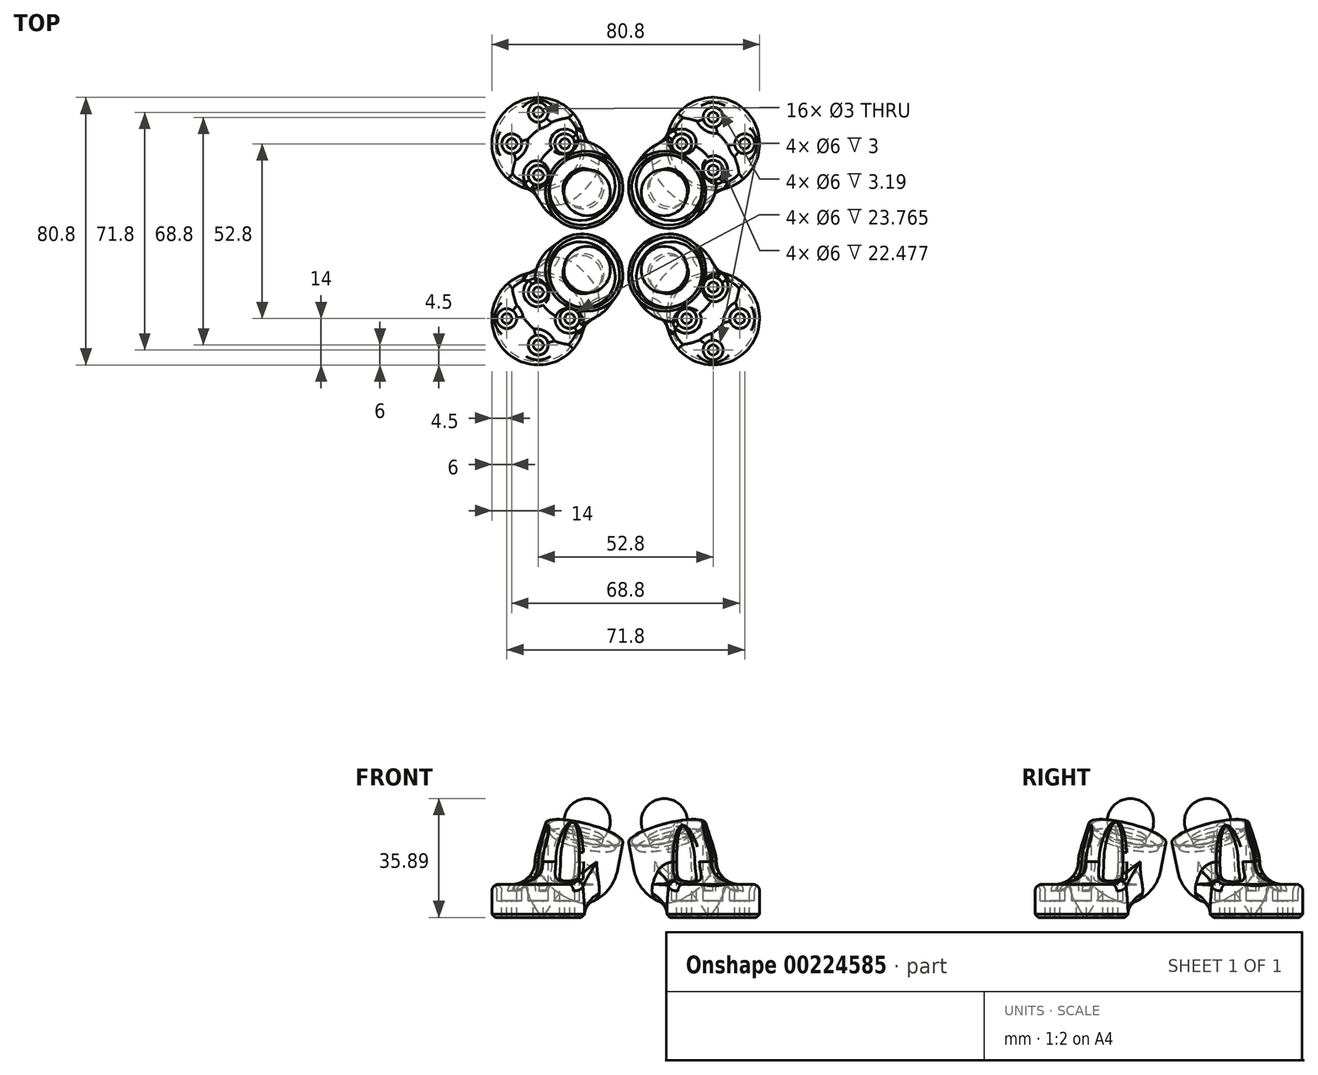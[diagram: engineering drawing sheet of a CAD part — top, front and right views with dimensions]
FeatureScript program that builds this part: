
annotation { "Feature Type Name" : "Feature", "Feature Type Description" : "" }
export const myFeature = defineFeature(function(context is Context, id is Id, definition is map)
    precondition{}
    {
        {
            var Q0;
            Q0=qCreatedBy(makeId("Top.planeOp"),FACE);
            var sketch = newSketch(context, id + "F0", { "sketchPlane" : qUnion([Q0])});
            skLineSegment(sketch, "E0", {"start": v(-39.6, -39.1) * mm, "end": v(-39.6, -104.05) * mm, "construction": true});
            skLineSegment(sketch, "E1", {"start": v(-66.97, -39.6) * mm, "end": v(-8.74, -39.6) * mm, "construction": true});
            skCircle(sketch, "E2", {"center": v(-39.6, -31.6) * mm, "radius": 1.5 * mm});
            skCircle(sketch, "E3", {"center": v(-39.6, -47.6) * mm, "radius": 1.5 * mm});
            skCircle(sketch, "E4", {"center": v(-49.1, -39.6) * mm, "radius": 1.5 * mm});
            skCircle(sketch, "E5", {"center": v(-30.1, -39.6) * mm, "radius": 1.5 * mm});
            skCircle(sketch, "E6", {"center": v(-39.6, -39.6) * mm, "radius": 14 * mm});
            skCircle(sketch, "E7", {"center": v(-49.1, -39.6) * mm, "radius": 3 * mm});
            skCircle(sketch, "E8", {"center": v(-39.6, -47.6) * mm, "radius": 3 * mm});
            skCircle(sketch, "E9", {"center": v(-30.1, -39.6) * mm, "radius": 3 * mm});
            skCircle(sketch, "E10", {"center": v(-39.6, -31.6) * mm, "radius": 3 * mm});
            skSolve(sketch);
        }
        {
            var Q0;
            Q0=qCreatedBy(makeId("Top.planeOp"),FACE);
            var sketch = newSketch(context, id + "F1", { "sketchPlane" : qUnion([Q0])});
            skLineSegment(sketch, "E11.bottom", {"start": v(53, -53) * mm, "end": v(-53, -53) * mm, "construction": true});
            skLineSegment(sketch, "E11.top", {"start": v(53, 53) * mm, "end": v(-53, 53) * mm, "construction": true});
            skLineSegment(sketch, "E11.left", {"start": v(53, -53) * mm, "end": v(53, 53) * mm, "construction": true});
            skLineSegment(sketch, "E11.right", {"start": v(-53, -53) * mm, "end": v(-53, 53) * mm, "construction": true});
            skPoint(sketch, "E11.middle", {"position": v(0, 0) * mm});
            skLineSegment(sketch, "E12", {"start": v(53, 53) * mm, "end": v(-53, -53) * mm, "construction": true});
            skLineSegment(sketch, "E13", {"start": v(-53, 53) * mm, "end": v(53, -53) * mm, "construction": true});
            skCircle(sketch, "E14", {"center": v(53, 38) * mm, "radius": 3 * mm});
            skCircle(sketch, "E15", {"center": v(53, 38) * mm, "radius": 1.4 * mm});
            skLineSegment(sketch, "E16", {"start": v(53, 38) * mm, "end": v(57.2, 42.2) * mm, "construction": true});
            skLineSegment(sketch, "E17", {"start": v(57.2, 0) * mm, "end": v(57.2, 42.2) * mm});
            skLineSegment(sketch, "E18", {"start": v(53, 38) * mm, "end": v(49.8, 34.8) * mm, "construction": true});
            skLineSegment(sketch, "E19", {"start": v(49.8, 0) * mm, "end": v(49.8, 34.8) * mm});
            skPoint(sketch, "E19.startSnap0", {"position": v(53, 0) * mm});
            skLineSegment(sketch, "E20", {"start": v(57.2, 42.2) * mm, "end": v(49.7, 49.7) * mm});
            skLineSegment(sketch, "E21", {"start": v(49.8, 34.8) * mm, "end": v(42.3, 42.3) * mm});
            skLineSegment(sketch, "E22", {"start": v(53, 38) * mm, "end": v(45.5, 45.5) * mm, "construction": true});
            skLineSegment(sketch, "E23.MirrorCS", {"start": v(42.2, 57.2) * mm, "end": v(49.7, 49.7) * mm});
            skLineSegment(sketch, "E24.MirrorCS", {"start": v(0, 49.8) * mm, "end": v(34.8, 49.8) * mm});
            skPoint(sketch, "E25.MirrorP", {"position": v(0, 53) * mm});
            skLineSegment(sketch, "E26.MirrorCS", {"start": v(0, 57.2) * mm, "end": v(42.2, 57.2) * mm});
            skLineSegment(sketch, "E27.MirrorCS", {"start": v(34.8, 49.8) * mm, "end": v(42.3, 42.3) * mm});
            skCircle(sketch, "E28.MirrorC", {"center": v(38, 53) * mm, "radius": 3 * mm});
            skCircle(sketch, "E29.MirrorC", {"center": v(38, 53) * mm, "radius": 1.4 * mm});
            skLineSegment(sketch, "E30.MirrorCS", {"start": v(38, 53) * mm, "end": v(34.8, 49.8) * mm, "construction": true});
            skLineSegment(sketch, "E31.MirrorCS", {"start": v(38, 53) * mm, "end": v(42.2, 57.2) * mm, "construction": true});
            skLineSegment(sketch, "E32.MirrorCS", {"start": v(38, 53) * mm, "end": v(45.5, 45.5) * mm, "construction": true});
            skCircle(sketch, "E33.MirrorC", {"center": v(-53, 38) * mm, "radius": 1.4 * mm});
            skCircle(sketch, "E34.MirrorC", {"center": v(-38, 53) * mm, "radius": 1.4 * mm});
            skLineSegment(sketch, "E35.MirrorCS", {"start": v(-38, 53) * mm, "end": v(-34.8, 49.8) * mm, "construction": true});
            skLineSegment(sketch, "E36.MirrorCS", {"start": v(-53, 38) * mm, "end": v(-49.8, 34.8) * mm, "construction": true});
            skLineSegment(sketch, "E37.MirrorCS", {"start": v(-53, 38) * mm, "end": v(-57.2, 42.2) * mm, "construction": true});
            skLineSegment(sketch, "E38.MirrorCS", {"start": v(-38, 53) * mm, "end": v(-42.2, 57.2) * mm, "construction": true});
            skLineSegment(sketch, "E39.MirrorCS", {"start": v(0, 49.8) * mm, "end": v(-34.8, 49.8) * mm});
            skLineSegment(sketch, "E40.MirrorCS", {"start": v(-49.8, 0) * mm, "end": v(-49.8, 34.8) * mm});
            skLineSegment(sketch, "E41.MirrorCS", {"start": v(-34.8, 49.8) * mm, "end": v(-42.3, 42.3) * mm});
            skLineSegment(sketch, "E42.MirrorCS", {"start": v(-57.2, 42.2) * mm, "end": v(-49.7, 49.7) * mm});
            skLineSegment(sketch, "E43.MirrorCS", {"start": v(-57.2, 0) * mm, "end": v(-57.2, 42.2) * mm});
            skLineSegment(sketch, "E44.MirrorCS", {"start": v(0, 57.2) * mm, "end": v(-42.2, 57.2) * mm});
            skLineSegment(sketch, "E45.MirrorCS", {"start": v(-42.2, 57.2) * mm, "end": v(-49.7, 49.7) * mm});
            skCircle(sketch, "E46.MirrorC", {"center": v(-53, 38) * mm, "radius": 3 * mm});
            skLineSegment(sketch, "E47.MirrorCS", {"start": v(-49.8, 34.8) * mm, "end": v(-42.3, 42.3) * mm});
            skPoint(sketch, "E48.MirrorP", {"position": v(-53, 0) * mm});
            skCircle(sketch, "E49.MirrorC", {"center": v(-38, 53) * mm, "radius": 3 * mm});
            skLineSegment(sketch, "E50.MirrorCS", {"start": v(-53, 38) * mm, "end": v(-45.5, 45.5) * mm, "construction": true});
            skLineSegment(sketch, "E51.MirrorCS", {"start": v(-38, 53) * mm, "end": v(-45.5, 45.5) * mm, "construction": true});
            skCircle(sketch, "E52.MirrorC", {"center": v(-38, -53) * mm, "radius": 1.4 * mm});
            skCircle(sketch, "E53.MirrorC", {"center": v(-53, -38) * mm, "radius": 1.4 * mm});
            skCircle(sketch, "E54.MirrorC", {"center": v(38, -53) * mm, "radius": 1.4 * mm});
            skCircle(sketch, "E55.MirrorC", {"center": v(53, -38) * mm, "radius": 1.4 * mm});
            skLineSegment(sketch, "E56.MirrorCS", {"start": v(-38, -53) * mm, "end": v(-34.8, -49.8) * mm, "construction": true});
            skLineSegment(sketch, "E57.MirrorCS", {"start": v(-53, -38) * mm, "end": v(-49.8, -34.8) * mm, "construction": true});
            skLineSegment(sketch, "E58.MirrorCS", {"start": v(38, -53) * mm, "end": v(34.8, -49.8) * mm, "construction": true});
            skLineSegment(sketch, "E59.MirrorCS", {"start": v(53, -38) * mm, "end": v(49.8, -34.8) * mm, "construction": true});
            skLineSegment(sketch, "E60.MirrorCS", {"start": v(-53, -38) * mm, "end": v(-57.2, -42.2) * mm, "construction": true});
            skLineSegment(sketch, "E61.MirrorCS", {"start": v(38, -53) * mm, "end": v(42.2, -57.2) * mm, "construction": true});
            skLineSegment(sketch, "E62.MirrorCS", {"start": v(53, -38) * mm, "end": v(57.2, -42.2) * mm, "construction": true});
            skLineSegment(sketch, "E63.MirrorCS", {"start": v(-38, -53) * mm, "end": v(-42.2, -57.2) * mm, "construction": true});
            skPoint(sketch, "E64.MirrorP", {"position": v(0, -53) * mm});
            skLineSegment(sketch, "E65.MirrorCS", {"start": v(0, -49.8) * mm, "end": v(34.8, -49.8) * mm});
            skLineSegment(sketch, "E66.MirrorCS", {"start": v(0, -49.8) * mm, "end": v(-34.8, -49.8) * mm});
            skLineSegment(sketch, "E67.MirrorCS", {"start": v(-49.8, 0) * mm, "end": v(-49.8, -34.8) * mm});
            skLineSegment(sketch, "E68.MirrorCS", {"start": v(49.8, 0) * mm, "end": v(49.8, -34.8) * mm});
            skLineSegment(sketch, "E69.MirrorCS", {"start": v(-49.8, -34.8) * mm, "end": v(-42.3, -42.3) * mm});
            skCircle(sketch, "E70.MirrorC", {"center": v(-53, -38) * mm, "radius": 3 * mm});
            skCircle(sketch, "E71.MirrorC", {"center": v(38, -53) * mm, "radius": 3 * mm});
            skLineSegment(sketch, "E72.MirrorCS", {"start": v(57.2, -42.2) * mm, "end": v(49.7, -49.7) * mm});
            skLineSegment(sketch, "E73.MirrorCS", {"start": v(49.8, -34.8) * mm, "end": v(42.3, -42.3) * mm});
            skCircle(sketch, "E74.MirrorC", {"center": v(53, -38) * mm, "radius": 3 * mm});
            skLineSegment(sketch, "E75.MirrorCS", {"start": v(-42.2, -57.2) * mm, "end": v(-49.7, -49.7) * mm});
            skLineSegment(sketch, "E76.MirrorCS", {"start": v(57.2, 0) * mm, "end": v(57.2, -42.2) * mm});
            skCircle(sketch, "E77.MirrorC", {"center": v(-38, -53) * mm, "radius": 3 * mm});
            skLineSegment(sketch, "E78.MirrorCS", {"start": v(-57.2, -42.2) * mm, "end": v(-49.7, -49.7) * mm});
            skLineSegment(sketch, "E79.MirrorCS", {"start": v(42.2, -57.2) * mm, "end": v(49.7, -49.7) * mm});
            skLineSegment(sketch, "E80.MirrorCS", {"start": v(0, -57.2) * mm, "end": v(-42.2, -57.2) * mm});
            skLineSegment(sketch, "E81.MirrorCS", {"start": v(-34.8, -49.8) * mm, "end": v(-42.3, -42.3) * mm});
            skLineSegment(sketch, "E82.MirrorCS", {"start": v(34.8, -49.8) * mm, "end": v(42.3, -42.3) * mm});
            skLineSegment(sketch, "E83.MirrorCS", {"start": v(-57.2, 0) * mm, "end": v(-57.2, -42.2) * mm});
            skLineSegment(sketch, "E84.MirrorCS", {"start": v(0, -57.2) * mm, "end": v(42.2, -57.2) * mm});
            skLineSegment(sketch, "E85.MirrorCS", {"start": v(-38, -53) * mm, "end": v(-45.5, -45.5) * mm, "construction": true});
            skLineSegment(sketch, "E86.MirrorCS", {"start": v(-53, -38) * mm, "end": v(-45.5, -45.5) * mm, "construction": true});
            skLineSegment(sketch, "E87.MirrorCS", {"start": v(53, -38) * mm, "end": v(45.5, -45.5) * mm, "construction": true});
            skLineSegment(sketch, "E88.MirrorCS", {"start": v(38, -53) * mm, "end": v(45.5, -45.5) * mm, "construction": true});
            skLineSegment(sketch, "E89", {"start": v(34.8, -49.8) * mm, "end": v(34.8, -57.2) * mm});
            skLineSegment(sketch, "E90", {"start": v(34.8, 49.8) * mm, "end": v(34.8, 57.2) * mm});
            skLineSegment(sketch, "E91", {"start": v(-34.8, 49.8) * mm, "end": v(-34.8, 57.2) * mm});
            skLineSegment(sketch, "E92", {"start": v(-34.8, -49.8) * mm, "end": v(-34.8, -57.2) * mm});
            skLineSegment(sketch, "E93", {"start": v(-42.3, 42.3) * mm, "end": v(-42.3, -42.3) * mm});
            skSolve(sketch);
        }
        {
            var Q0;
            Q0=qCreatedBy(makeId("Front.planeOp"),FACE);
            var sketch = newSketch(context, id + "F2", { "sketchPlane" : qUnion([Q0])});
            skLineSegment(sketch, "E94", {"start": v(0, 0) * mm, "end": v(0, 2) * mm});
            skSolve(sketch);
        }
        {
            var Q0;
            Q0=sQuery(id+"F2.wireOp",EDGE,"E94");
            extrude(context, id + "F3", {"bodyType" : ExtendedToolBodyType.SURFACE, "surfaceEntities" : qUnion([Q0]), "depth" : 1 * mm});
        }
        {
            var Q0;
            Q0=qCreatedBy(makeId("Front.planeOp"),FACE);
            var Q1;
            Q1=sQuery(id+"F2.wireOp",EDGE,"E94");
            cPlane(context, id + "F4", {"entities" : qUnion([Q0, Q1]), "cplaneType" : CPlaneType.LINE_ANGLE, "offset" : 25 * mm, "angle" : 45 * degree, "width" : 150 * mm, "height" : 150 * mm});
        }
        {
            var Q0;
            Q0=qCreatedBy(id+"F4.planeOp",FACE);
            var sketch = newSketch(context, id + "F5", { "sketchPlane" : qUnion([Q0])});
            skLineSegment(sketch, "E95", {"start": v(-2, 0) * mm, "end": v(0, 0) * mm});
            skSolve(sketch);
        }
        {
            var Q0;
            Q0=qCreatedBy(id+"F4.planeOp",FACE);
            var sketch = newSketch(context, id + "F6", { "sketchPlane" : qUnion([Q0])});
            skLineSegment(sketch, "E96", {"start": v(70, 0) * mm, "end": v(70, 20) * mm, "construction": true});
            skCircle(sketch, "E97", {"center": v(70, 20) * mm, "radius": 7 * mm});
            skLineSegment(sketch, "E98", {"start": v(70, 0) * mm, "end": v(70, 15.12) * mm});
            skLineSegment(sketch, "E99", {"start": v(70, -15.12) * mm, "end": v(70, -15.12) * mm});
            skLineSegment(sketch, "E100", {"start": v(70, 15.12) * mm, "end": v(70, 27) * mm});
            skArc(sketch, "E101", {"start": v(70, -5.87) * mm, "mid": v(81.14, 0.97) * mm, "end": v(80.2, 14) * mm});
            skLineSegment(sketch, "E102", {"start": v(76, 9.37) * mm, "end": v(76, 16.4) * mm});
            skLineSegment(sketch, "E103", {"start": v(80.2, 14) * mm, "end": v(76, 14) * mm});
            skLineSegment(sketch, "E104", {"start": v(76, 16.4) * mm, "end": v(81.03, 16.4) * mm});
            skLineSegment(sketch, "E105", {"start": v(81.03, 16.4) * mm, "end": v(80.2, 14) * mm});
            skLineSegment(sketch, "E106", {"start": v(81.03, 16.4) * mm, "end": v(82.03, 16.4) * mm});
            skLineSegment(sketch, "E107", {"start": v(82.03, 16.4) * mm, "end": v(82.5, 7.38) * mm});
            skLineSegment(sketch, "E108", {"start": v(70, -5.87) * mm, "end": v(70, 0) * mm});
            skSolve(sketch);
        }
        {
            var Q0;
            {var subQ4=sQuery(id+"F6.wireOp",EDGE,"E100");Q0=makeQuery(id+"F6.imprint","IMPRINT",FACE,{"disambiguationData":[TD([[makeQuery(id+"F6.imprint","IMPRINT",EDGE,{"derivedFrom":subQ4}),-1.0]])]});}
            var Q1;
            {var subQ4=sQuery(id+"F6.wireOp",EDGE,"E103");Q1=makeQuery(id+"F6.imprint","IMPRINT",FACE,{"disambiguationData":[TD([[makeQuery(id+"F6.imprint","IMPRINT",EDGE,{"derivedFrom":subQ4}),1.0]])]});}
            var Q2;
            {var subQ0=sQuery(id+"F6.wireOp",EDGE,"E105");Q2=makeQuery(id+"F6.imprint","IMPRINT",FACE,{"disambiguationData":[TD([[makeQuery(id+"F6.imprint","IMPRINT",EDGE,{"derivedFrom":subQ0}),1.0]])]});}
            var Q3;
            Q3=sQuery(id+"F6.wireOp",EDGE,"E100");
            revolve(context, id + "F7", {"entities" : qUnion([Q0, Q1, Q2]), "axis" : qUnion([Q3]), "revolveType" : RevolveType.FULL});
        }
        {
            var Q0;
            Q0=makeQuery(id+"F7.opRevolve","SWEPT_BODY",BODY,{"disambiguationData":[OSD([sQuery(id+"F6.wireOp",EDGE,"E97"),sQuery(id+"F6.wireOp",EDGE,"f09eb4f5-6c82-4df3-bae4-9ba73b9464a2"),sQuery(id+"F6.wireOp",EDGE,"19ab945a-1405-4e05-9aeb-33d9ebbb6d5e"),sQuery(id+"F6.wireOp",EDGE,"E98"),sQuery(id+"F6.wireOp",EDGE,"6Gewuh9S-kY6R-dueU-HYYT-GC4jgHSk6Dqt"),sQuery(id+"F6.wireOp",EDGE,"E100"),sQuery(id+"F6.wireOp",EDGE,"E101")])]});
            var Q1;
            Q1=sQuery(id+"F1.wireOp",EDGE,"E78.MirrorCS");
            transform(context, id + "F8", {"entities" : qUnion([Q0]), "transformType" : TransformType.ROTATION, "transformAxis" : qUnion([Q1]), "angle" : 20 * degree, "makeCopy" : false});
        }
        {
            var Q0;
            Q0=makeQuery(id+"F3.opExtrude","SWEPT_BODY",BODY,{"disambiguationData":[OSD([sQuery(id+"F2.wireOp",EDGE,"E94")])]});
            deleteBodies(context, id + "F9", {"entities" : qUnion([Q0])});
        }
        {
            var Q0;
            Q0=makeQuery(id+"F0.imprint","IMPRINT",FACE,{"disambiguationData":[TD([[makeQuery(id+"F0.imprint","IMPRINT",EDGE,{"derivedFrom":sQuery(id+"F0.wireOp",EDGE,"E6")}),1.0]])]});
            var Q1;
            Q1=makeQuery(id+"F0.imprint","IMPRINT",FACE,{"disambiguationData":[TD([[makeQuery(id+"F0.imprint","IMPRINT",EDGE,{"derivedFrom":sQuery(id+"F0.wireOp",EDGE,"E4")}),-1.0]])]});
            var Q2;
            Q2=makeQuery(id+"F0.imprint","IMPRINT",FACE,{"disambiguationData":[TD([[makeQuery(id+"F0.imprint","IMPRINT",EDGE,{"derivedFrom":sQuery(id+"F0.wireOp",EDGE,"E2")}),-1.0]])]});
            var Q3;
            Q3=makeQuery(id+"F0.imprint","IMPRINT",FACE,{"disambiguationData":[TD([[makeQuery(id+"F0.imprint","IMPRINT",EDGE,{"derivedFrom":sQuery(id+"F0.wireOp",EDGE,"E5")}),-1.0]])]});
            var Q4;
            Q4=makeQuery(id+"F0.imprint","IMPRINT",FACE,{"disambiguationData":[TD([[makeQuery(id+"F0.imprint","IMPRINT",EDGE,{"derivedFrom":sQuery(id+"F0.wireOp",EDGE,"E3")}),-1.0]])]});
            extrude(context, id + "F10", {"entities" : qUnion([Q0, Q1, Q2, Q3, Q4]), "operationType" : NewBodyOperationType.ADD, "oppositeDirection" : true, "depth" : 10 * mm, "offsetDistance" : 25 * mm});
        }
        {
            var Q0;
            Q0=makeQuery(id+"F10.boolean.opBoolean","INTERSECT",EDGE,{"derivedFrom":[makeQuery(id+"F7.opRevolve","SWEPT_FACE",FACE,{"disambiguationData":[OSD([sQuery(id+"F6.wireOp",EDGE,"E101")])]}),makeQuery(id+"F10.opExtrude","SWEPT_FACE",FACE,{"disambiguationData":[OSD([sQuery(id+"F0.wireOp",EDGE,"E6")])]})]});
            fillet(context, id + "F11", {"entities" : qUnion([Q0]), "radius" : 10 * mm, "tangentPropagation" : true, "allowEdgeOverflow" : false});
        }
        {
            var Q0;
            Q0=makeQuery(id+"F0.imprint","IMPRINT",FACE,{"disambiguationData":[TD([[makeQuery(id+"F0.imprint","IMPRINT",EDGE,{"derivedFrom":sQuery(id+"F0.wireOp",EDGE,"E4")}),-1.0]])]});
            var Q1;
            Q1=makeQuery(id+"F0.imprint","IMPRINT",FACE,{"disambiguationData":[TD([[makeQuery(id+"F0.imprint","IMPRINT",EDGE,{"derivedFrom":sQuery(id+"F0.wireOp",EDGE,"E4")}),1.0]])]});
            var Q2;
            Q2=makeQuery(id+"F0.imprint","IMPRINT",FACE,{"disambiguationData":[TD([[makeQuery(id+"F0.imprint","IMPRINT",EDGE,{"derivedFrom":sQuery(id+"F0.wireOp",EDGE,"E2")}),1.0]])]});
            var Q3;
            Q3=makeQuery(id+"F0.imprint","IMPRINT",FACE,{"disambiguationData":[TD([[makeQuery(id+"F0.imprint","IMPRINT",EDGE,{"derivedFrom":sQuery(id+"F0.wireOp",EDGE,"E2")}),-1.0]])]});
            var Q4;
            Q4=makeQuery(id+"F0.imprint","IMPRINT",FACE,{"disambiguationData":[TD([[makeQuery(id+"F0.imprint","IMPRINT",EDGE,{"derivedFrom":sQuery(id+"F0.wireOp",EDGE,"E5")}),-1.0]])]});
            var Q5;
            Q5=makeQuery(id+"F0.imprint","IMPRINT",FACE,{"disambiguationData":[TD([[makeQuery(id+"F0.imprint","IMPRINT",EDGE,{"derivedFrom":sQuery(id+"F0.wireOp",EDGE,"E5")}),1.0]])]});
            var Q6;
            Q6=makeQuery(id+"F0.imprint","IMPRINT",FACE,{"disambiguationData":[TD([[makeQuery(id+"F0.imprint","IMPRINT",EDGE,{"derivedFrom":sQuery(id+"F0.wireOp",EDGE,"E3")}),-1.0]])]});
            var Q7;
            Q7=makeQuery(id+"F0.imprint","IMPRINT",FACE,{"disambiguationData":[TD([[makeQuery(id+"F0.imprint","IMPRINT",EDGE,{"derivedFrom":sQuery(id+"F0.wireOp",EDGE,"E3")}),1.0]])]});
            extrude(context, id + "F12", {"entities" : qUnion([Q0, Q1, Q2, Q3, Q4, Q5, Q6, Q7]), "operationType" : NewBodyOperationType.REMOVE, "oppositeDirection" : true, "depth" : 5 * mm, "offsetDistance" : 25 * mm});
        }
        {
            var Q0;
            Q0=makeQuery(id+"F0.imprint","IMPRINT",FACE,{"disambiguationData":[TD([[makeQuery(id+"F0.imprint","IMPRINT",EDGE,{"derivedFrom":sQuery(id+"F0.wireOp",EDGE,"E3")}),-1.0]])]});
            var Q1;
            Q1=makeQuery(id+"F0.imprint","IMPRINT",FACE,{"disambiguationData":[TD([[makeQuery(id+"F0.imprint","IMPRINT",EDGE,{"derivedFrom":sQuery(id+"F0.wireOp",EDGE,"E3")}),1.0]])]});
            var Q2;
            Q2=makeQuery(id+"F0.imprint","IMPRINT",FACE,{"disambiguationData":[TD([[makeQuery(id+"F0.imprint","IMPRINT",EDGE,{"derivedFrom":sQuery(id+"F0.wireOp",EDGE,"E4")}),1.0]])]});
            var Q3;
            Q3=makeQuery(id+"F0.imprint","IMPRINT",FACE,{"disambiguationData":[TD([[makeQuery(id+"F0.imprint","IMPRINT",EDGE,{"derivedFrom":sQuery(id+"F0.wireOp",EDGE,"E4")}),-1.0]])]});
            var Q4;
            Q4=makeQuery(id+"F0.imprint","IMPRINT",FACE,{"disambiguationData":[TD([[makeQuery(id+"F0.imprint","IMPRINT",EDGE,{"derivedFrom":sQuery(id+"F0.wireOp",EDGE,"E2")}),-1.0]])]});
            var Q5;
            Q5=makeQuery(id+"F0.imprint","IMPRINT",FACE,{"disambiguationData":[TD([[makeQuery(id+"F0.imprint","IMPRINT",EDGE,{"derivedFrom":sQuery(id+"F0.wireOp",EDGE,"E2")}),1.0]])]});
            var Q6;
            Q6=makeQuery(id+"F0.imprint","IMPRINT",FACE,{"disambiguationData":[TD([[makeQuery(id+"F0.imprint","IMPRINT",EDGE,{"derivedFrom":sQuery(id+"F0.wireOp",EDGE,"E5")}),1.0]])]});
            var Q7;
            Q7=makeQuery(id+"F0.imprint","IMPRINT",FACE,{"disambiguationData":[TD([[makeQuery(id+"F0.imprint","IMPRINT",EDGE,{"derivedFrom":sQuery(id+"F0.wireOp",EDGE,"E5")}),-1.0]])]});
            extrude(context, id + "F13", {"entities" : qUnion([Q0, Q1, Q2, Q3, Q4, Q5, Q6, Q7]), "operationType" : NewBodyOperationType.REMOVE, "depth" : 25 * mm, "offsetDistance" : 25 * mm});
        }
        {
            var Q0;
            {var subQ0=makeQuery(id+"F7.opRevolve","SWEPT_FACE",FACE,{"disambiguationData":[OSD([sQuery(id+"F6.wireOp",EDGE,"E101")])]});var subQ1=makeQuery(id+"F10.opExtrude","CAP_FACE",FACE,{"disambiguationData":[OSD([sQuery(id+"F0.wireOp",EDGE,"E6")])],"isStart":true});Q0=makeQuery(id+"F12.boolean.opBoolean","SPLIT",EDGE,{"disambiguationData":[TD([subQ0,subQ1,makeQuery(id+"F12.opExtrude","SWEPT_FACE",FACE,{"disambiguationData":[OSD([sQuery(id+"F0.wireOp",EDGE,"E7")])]}),makeQuery(id+"F12.opExtrude","SWEPT_FACE",FACE,{"disambiguationData":[OSD([sQuery(id+"F0.wireOp",EDGE,"E8")])]})])],"derivedFrom":makeQuery(id+"F10.boolean.opBoolean","INTERSECT",EDGE,{"derivedFrom":[subQ0,subQ1]})});}
            var Q1;
            {var subQ0=sQuery(id+"F6.wireOp",EDGE,"E101");var subQ1=makeQuery(id+"F7.opRevolve","SWEPT_FACE",FACE,{"disambiguationData":[OSD([subQ0])]});var subQ2=sQuery(id+"F0.wireOp",EDGE,"E6");var subQ3=makeQuery(id+"F10.opExtrude","CAP_FACE",FACE,{"disambiguationData":[OSD([subQ2])],"isStart":true});Q1=makeQuery(id+"F12.boolean.opBoolean","SPLIT",EDGE,{"disambiguationData":[TD([subQ1,subQ3,makeQuery(id+"F11.opFillet","BLEND_FACE",FACE,{"disambiguationData":[OSD([subQ2,subQ0])]}),makeQuery(id+"F12.opExtrude","SWEPT_FACE",FACE,{"disambiguationData":[OSD([sQuery(id+"F0.wireOp",EDGE,"E7")])]})])],"derivedFrom":makeQuery(id+"F10.boolean.opBoolean","INTERSECT",EDGE,{"derivedFrom":[subQ1,subQ3]})});}
            var Q2;
            {var subQ0=sQuery(id+"F6.wireOp",EDGE,"E101");var subQ1=makeQuery(id+"F7.opRevolve","SWEPT_FACE",FACE,{"disambiguationData":[OSD([subQ0])]});var subQ2=sQuery(id+"F0.wireOp",EDGE,"E6");var subQ3=makeQuery(id+"F10.opExtrude","CAP_FACE",FACE,{"disambiguationData":[OSD([subQ2])],"isStart":true});Q2=makeQuery(id+"F12.boolean.opBoolean","SPLIT",EDGE,{"disambiguationData":[TD([subQ1,subQ3,makeQuery(id+"F11.opFillet","BLEND_FACE",FACE,{"disambiguationData":[OSD([subQ2,subQ0])]}),makeQuery(id+"F12.opExtrude","SWEPT_FACE",FACE,{"disambiguationData":[OSD([sQuery(id+"F0.wireOp",EDGE,"E8")])]})])],"derivedFrom":makeQuery(id+"F10.boolean.opBoolean","INTERSECT",EDGE,{"derivedFrom":[subQ1,subQ3]})});}
            fillet(context, id + "F14", {"entities" : qUnion([Q0, Q1, Q2]), "radius" : 7 * mm, "tangentPropagation" : true, "allowEdgeOverflow" : false});
        }
        {
            var Q0;
            Q0=makeQuery(id+"F10.opExtrude","CAP_FACE",FACE,{"disambiguationData":[OSD([sQuery(id+"F0.wireOp",EDGE,"E6")])],"isStart":true});
            fillet(context, id + "F15", {"entities" : qUnion([Q0]), "radius" : 2 * mm, "tangentPropagation" : true, "allowEdgeOverflow" : false});
        }
        {
            var Q0;
            {var subQ0=makeQuery(id+"F12.opExtrude","SWEPT_FACE",FACE,{"disambiguationData":[OSD([sQuery(id+"F0.wireOp",EDGE,"E7")])]});var subQ1=sQuery(id+"F6.wireOp",EDGE,"E101");var subQ2=makeQuery(id+"F7.opRevolve","SWEPT_FACE",FACE,{"disambiguationData":[OSD([subQ1])]});var subQ3=sQuery(id+"F0.wireOp",EDGE,"E6");var subQ4=makeQuery(id+"F10.opExtrude","CAP_FACE",FACE,{"disambiguationData":[OSD([subQ3])],"isStart":true});Q0=makeQuery(id+"F14.opFillet","BLEND_EDGE",EDGE,{"blendedFrom":[makeQuery(id+"F12.boolean.opBoolean","SPLIT",EDGE,{"disambiguationData":[TD([subQ2,subQ4,makeQuery(id+"F11.opFillet","BLEND_FACE",FACE,{"disambiguationData":[OSD([subQ3,subQ1])]}),subQ0])],"derivedFrom":makeQuery(id+"F10.boolean.opBoolean","INTERSECT",EDGE,{"derivedFrom":[subQ2,subQ4]})}),makeQuery(id+"F12.boolean.opBoolean","COPY",FACE,{"derivedFrom":subQ0})],"blendedInto":[makeQuery(id+"F12.boolean.opBoolean","COPY",FACE,{"derivedFrom":subQ0})]});}
            var Q1;
            {var subQ0=sQuery(id+"F6.wireOp",EDGE,"E101");var subQ1=makeQuery(id+"F7.opRevolve","SWEPT_FACE",FACE,{"disambiguationData":[OSD([subQ0])]});var subQ2=sQuery(id+"F0.wireOp",EDGE,"E6");var subQ3=makeQuery(id+"F10.opExtrude","CAP_FACE",FACE,{"disambiguationData":[OSD([subQ2])],"isStart":true});Q1=makeQuery(id+"F14.opFillet","BLEND_EDGE",EDGE,{"blendedFrom":[makeQuery(id+"F12.boolean.opBoolean","SPLIT",EDGE,{"disambiguationData":[TD([subQ1,subQ3,makeQuery(id+"F11.opFillet","BLEND_FACE",FACE,{"disambiguationData":[OSD([subQ2,subQ0])]}),makeQuery(id+"F12.opExtrude","SWEPT_FACE",FACE,{"disambiguationData":[OSD([sQuery(id+"F0.wireOp",EDGE,"E7")])]})])],"derivedFrom":makeQuery(id+"F10.boolean.opBoolean","INTERSECT",EDGE,{"derivedFrom":[subQ1,subQ3]})}),makeQuery(id+"F12.boolean.opBoolean","COPY",FACE,{"derivedFrom":makeQuery(id+"F12.opExtrude","SWEPT_FACE",FACE,{"disambiguationData":[OSD([sQuery(id+"F0.wireOp",EDGE,"E8")])]})})],"blendedInto":[makeQuery(id+"F12.boolean.opBoolean","COPY",FACE,{"derivedFrom":makeQuery(id+"F12.opExtrude","SWEPT_FACE",FACE,{"disambiguationData":[OSD([sQuery(id+"F0.wireOp",EDGE,"E8")])]})})]});}
            fillet(context, id + "F16", {"entities" : qUnion([Q0, Q1]), "radius" : 1 * mm, "tangentPropagation" : true, "allowEdgeOverflow" : false});
        }
        {
            var Q0;
            Q0=makeQuery(id+"F10.opExtrude","CAP_EDGE",EDGE,{"disambiguationData":[OSD([sQuery(id+"F0.wireOp",EDGE,"E6")])],"isStart":false});
            chamfer(context, id + "F17", {"entities" : qUnion([Q0]), "width" : 1 * mm, "tangentPropagation" : true});
        }
        {
            var Q0;
            Q0=qCreatedBy(makeId("Front.planeOp"),FACE);
            cPlane(context, id + "F18", {"entities" : qUnion([Q0]), "cplaneType" : CPlaneType.OFFSET, "offset" : 66 * mm, "width" : 150 * mm, "height" : 150 * mm});
        }
        {
            var Q0;
            Q0=qCreatedBy(id+"F18.planeOp",FACE);
            var sketch = newSketch(context, id + "F19", { "sketchPlane" : qUnion([Q0])});
            skLineSegment(sketch, "E109", {"start": v(-66, 0) * mm, "end": v(-66, 10) * mm, "construction": true});
            skSolve(sketch);
        }
        {
            var Q0;
            Q0=makeQuery(id+"F7.opRevolve","SWEPT_BODY",BODY,{"disambiguationData":[OSD([sQuery(id+"F6.wireOp",EDGE,"E97"),sQuery(id+"F6.wireOp",EDGE,"E98"),sQuery(id+"F6.wireOp",EDGE,"E100"),sQuery(id+"F6.wireOp",EDGE,"E101"),sQuery(id+"F6.wireOp",EDGE,"E102"),sQuery(id+"F6.wireOp",EDGE,"E103"),sQuery(id+"F6.wireOp",EDGE,"E105"),sQuery(id+"F6.wireOp",EDGE,"E106"),sQuery(id+"F6.wireOp",EDGE,"E107"),sQuery(id+"F6.wireOp",EDGE,"E108")])]});
            var Q1;
            Q1=sQuery(id+"F19.wireOp",EDGE,"E109");
            circularPattern(context, id + "F20", {"entities" : qUnion([Q0]), "axis" : qUnion([Q1]), "angle" : 360 * degree, "instanceCount" : 4, "equalSpace" : true, "computeTransformsWithoutBuiltin" : true});
        }
    });
